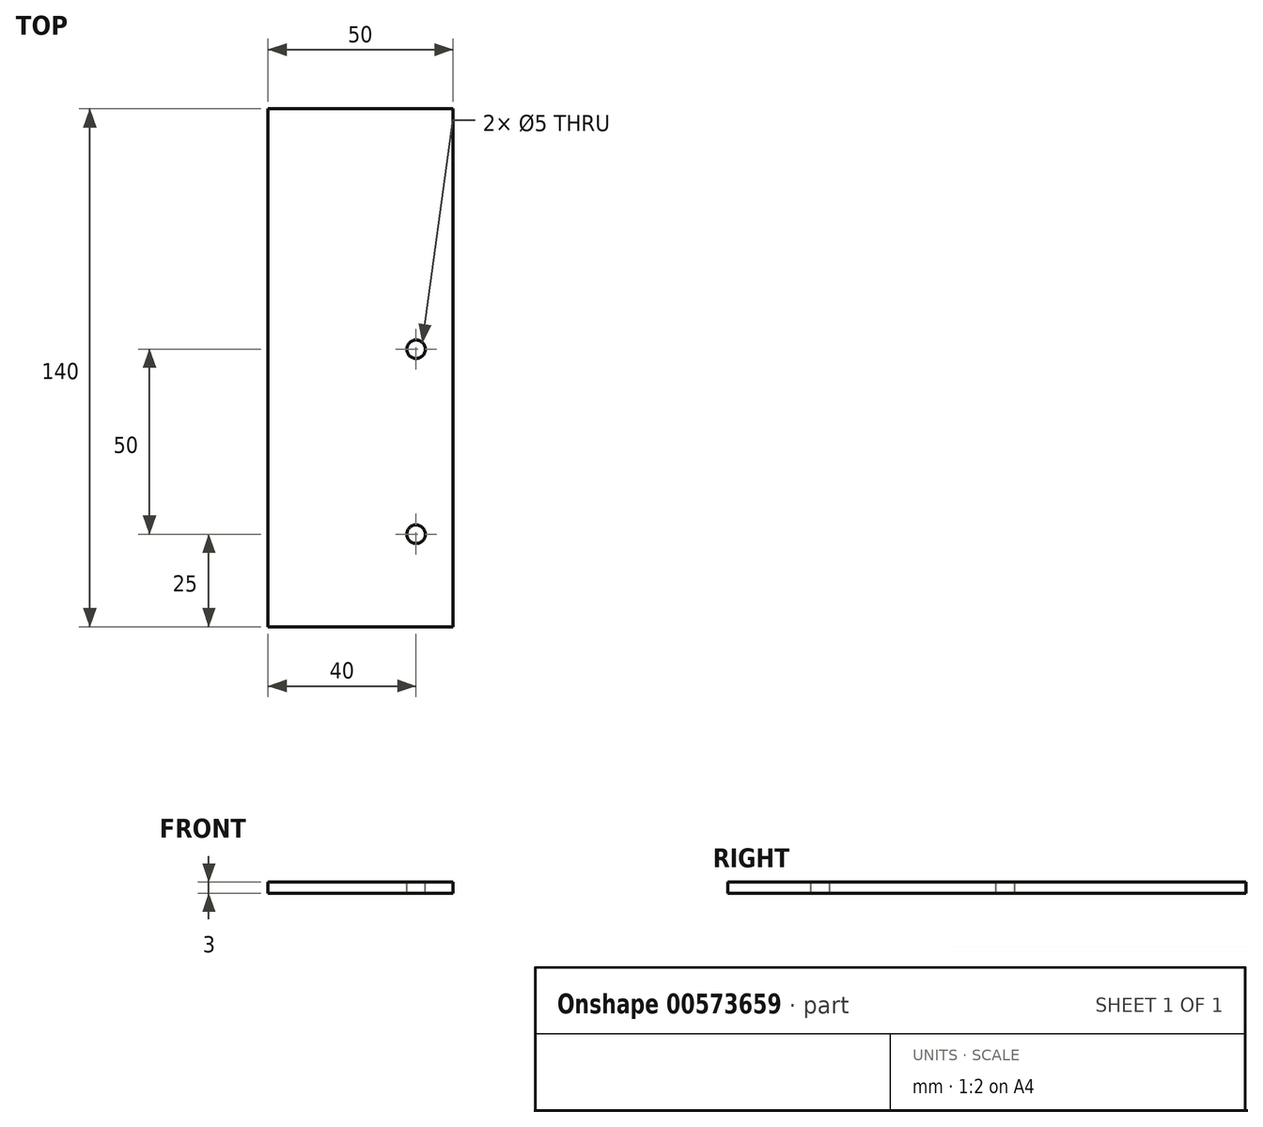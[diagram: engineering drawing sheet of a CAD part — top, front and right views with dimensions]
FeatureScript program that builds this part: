
annotation { "Feature Type Name" : "Feature", "Feature Type Description" : "" }
export const myFeature = defineFeature(function(context is Context, id is Id, definition is map)
    precondition{}
    {
        {
            var Q0;
            Q0=qCreatedBy(makeId("Top.planeOp"),FACE);
            var sketch = newSketch(context, id + "F0", { "sketchPlane" : qUnion([Q0])});
            skLineSegment(sketch, "E0.bottom", {"start": v(0, 0) * mm, "end": v(50, 0) * mm});
            skLineSegment(sketch, "E0.top", {"start": v(0, 140) * mm, "end": v(50, 140) * mm});
            skLineSegment(sketch, "E0.left", {"start": v(0, 0) * mm, "end": v(0, 140) * mm});
            skLineSegment(sketch, "E0.right", {"start": v(50, 0) * mm, "end": v(50, 140) * mm});
            skSolve(sketch);
        }
        {
            var Q0;
            Q0 = qSketchRegion(id + "F0", true);
            extrude(context, id + "F1", {"entities" : qUnion([Q0]), "depth" : 3 * mm, "offsetDistance" : 25 * mm});
        }
        {
            var Q0;
            Q0=makeQuery(id+"F1.opExtrude","CAP_FACE",FACE,{"disambiguationData":[OSD([sQuery(id+"F0.wireOp",EDGE,"E0.bottom"),sQuery(id+"F0.wireOp",EDGE,"E0.top"),sQuery(id+"F0.wireOp",EDGE,"E0.left"),sQuery(id+"F0.wireOp",EDGE,"E0.right")])],"isStart":false});
            var sketch = newSketch(context, id + "F2", { "sketchPlane" : qUnion([Q0])});
            skLineSegment(sketch, "E1", {"start": v(40, 25) * mm, "end": v(40, 75) * mm});
            skSolve(sketch);
        }
        {
            var Q0;
            Q0=makeQuery(id+"F2.imprint","IMPRINT",FACE,{"disambiguationData":[TD([[makeQuery(id+"F2.imprint","IMPRINT",EDGE,{"derivedFrom":makeQuery(id+"F1.opExtrude","CAP_EDGE",EDGE,{"disambiguationData":[OSD([sQuery(id+"F0.wireOp",EDGE,"E0.bottom")])],"isStart":false})}),1.0]])]});
            var sketch = newSketch(context, id + "F3", { "sketchPlane" : qUnion([Q0])});
            skSolve(sketch);
        }
        {
            var Q0;
            Q0=sQuery(id+"F2.wireOp",VERTEX,"E1.end");
            var Q1;
            Q1=sQuery(id+"F2.wireOp",VERTEX,"E1.start");
            var Q2;
            Q2=makeQuery(id+"F1.opExtrude","SWEPT_BODY",BODY,{"disambiguationData":[OSD([sQuery(id+"F0.wireOp",EDGE,"E0.bottom"),sQuery(id+"F0.wireOp",EDGE,"E0.top"),sQuery(id+"F0.wireOp",EDGE,"E0.left"),sQuery(id+"F0.wireOp",EDGE,"E0.right")])]});
            hole(context, id + "F4", {"style" : HoleStyle.SIMPLE, "endStyle" : HoleEndStyle.THROUGH, "holeDiameter" : 5 * mm, "isTappedThrough" : true, "tappedDepth" : 12 * mm, "tapClearance" : 3, "locations" : qUnion([Q0, Q1]), "scope" : qUnion([Q2])});
        }
        {
            var Q0;
            Q0=makeQuery(id+"F3.imprint","IMPRINT",FACE,{"disambiguationData":[TD([[makeQuery(id+"F3.imprint","IMPRINT",EDGE,{"derivedFrom":makeQuery(id+"F2.imprint","IMPRINT",EDGE,{"derivedFrom":makeQuery(id+"F1.opExtrude","CAP_EDGE",EDGE,{"disambiguationData":[OSD([sQuery(id+"F0.wireOp",EDGE,"E0.bottom")])],"isStart":false})})}),1.0]])]});
            var sketch = newSketch(context, id + "F5", { "sketchPlane" : qUnion([Q0])});
            skLineSegment(sketch, "E2", {"start": v(45, 75) * mm, "end": v(45, 20) * mm});
            skArc(sketch, "E3.0.startCap", {"start": v(42.5, 75) * mm, "mid": v(45, 77.5) * mm, "end": v(47.5, 75) * mm});
            skArc(sketch, "E3.0.endCap", {"start": v(47.5, 20) * mm, "mid": v(45, 17.5) * mm, "end": v(42.5, 20) * mm});
            skLineSegment(sketch, "E3.0.left", {"start": v(47.5, 75) * mm, "end": v(47.5, 20) * mm});
            skLineSegment(sketch, "E3.0.right", {"start": v(42.5, 75) * mm, "end": v(42.5, 20) * mm});
            skSolve(sketch);
        }
        {
            var Q0;
            Q0 = qSketchRegion(id + "F5", true);
            var sketch = newSketch(context, id + "F6", { "sketchPlane" : qUnion([Q0])});
            skSolve(sketch);
        }
    });
